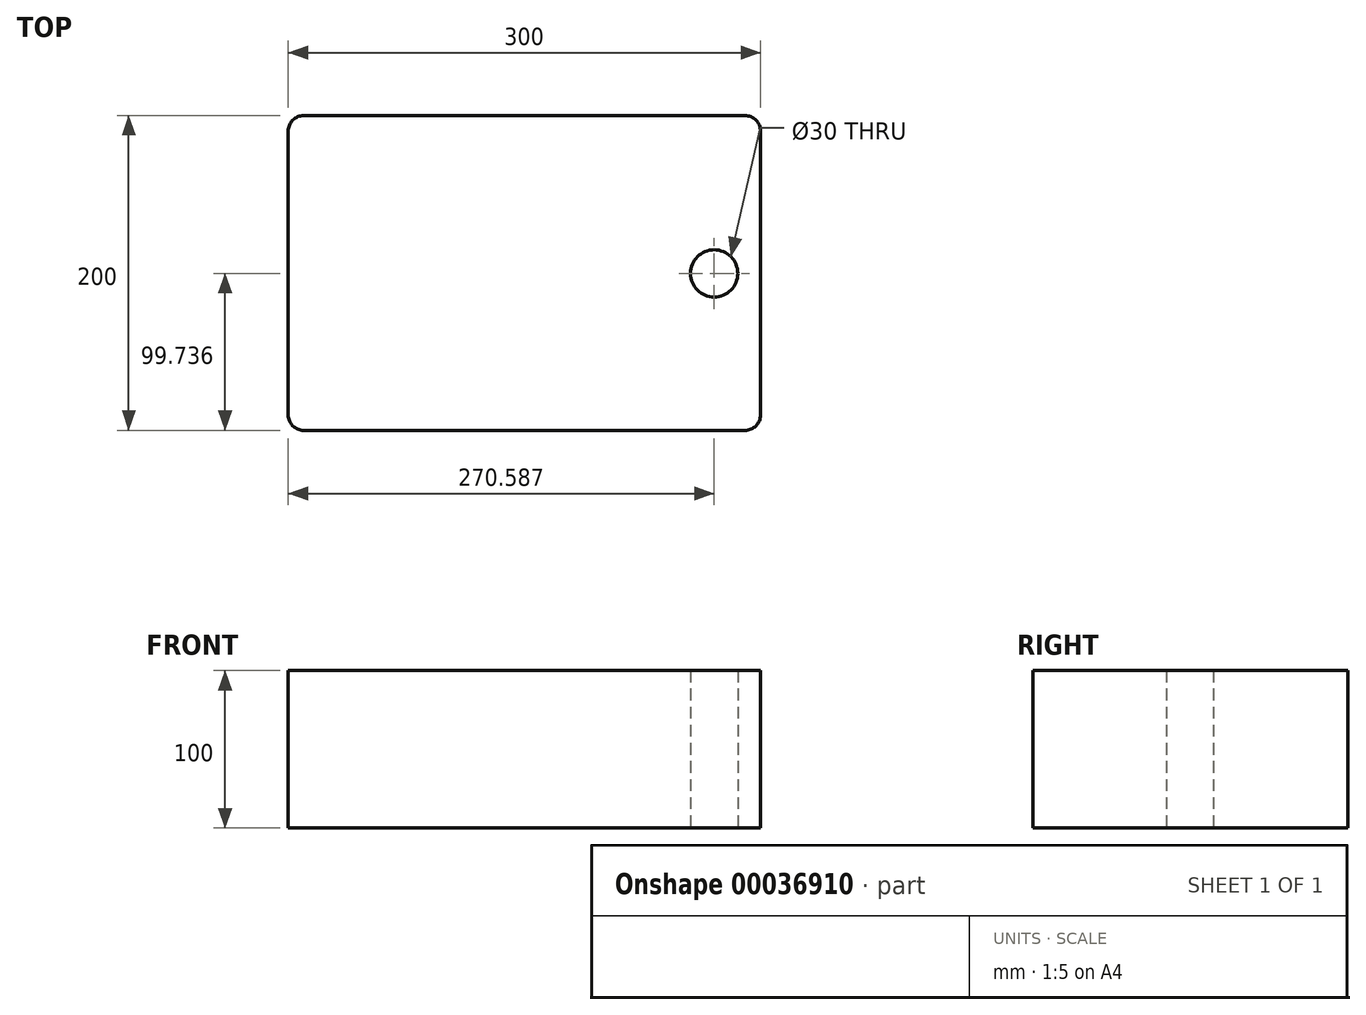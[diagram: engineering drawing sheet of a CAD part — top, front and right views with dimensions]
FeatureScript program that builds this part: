
annotation { "Feature Type Name" : "Feature", "Feature Type Description" : "" }
export const myFeature = defineFeature(function(context is Context, id is Id, definition is map)
    precondition{}
    {
        {
            var Q0;
            Q0=qCreatedBy(makeId("Top.planeOp"),FACE);
            var sketch = newSketch(context, id + "F0", { "sketchPlane" : qUnion([Q0])});
            skLineSegment(sketch, "E0.bottom", {"start": v(-154.92, 124.98) * mm, "end": v(145.08, 124.98) * mm});
            skLineSegment(sketch, "E0.top", {"start": v(-154.92, -75.02) * mm, "end": v(145.08, -75.02) * mm});
            skLineSegment(sketch, "E0.left", {"start": v(-154.92, 124.98) * mm, "end": v(-154.92, -75.02) * mm});
            skLineSegment(sketch, "E0.right", {"start": v(145.08, 124.98) * mm, "end": v(145.08, -75.02) * mm});
            skCircle(sketch, "E1", {"center": v(115.67, 24.72) * mm, "radius": 15 * mm});
            skSolve(sketch);
        }
        {
            var Q0;
            Q0=makeQuery(id+"F0.imprint","IMPRINT",FACE,{"disambiguationData":[TD([[makeQuery(id+"F0.imprint","IMPRINT",EDGE,{"derivedFrom":sQuery(id+"F0.wireOp",EDGE,"E0.bottom")}),-1.0]])]});
            extrude(context, id + "F1", {"entities" : qUnion([Q0]), "depth" : 100 * mm});
        }
        {
            var Q0;
            Q0=makeQuery(id+"F1.opExtrude","SWEPT_EDGE",EDGE,{"disambiguationData":[OSD([sQuery(id+"F0.wireOp",EDGE,"E0.bottom"),sQuery(id+"F0.wireOp",EDGE,"E0.left")])]});
            var Q1;
            Q1=makeQuery(id+"F1.opExtrude","SWEPT_EDGE",EDGE,{"disambiguationData":[OSD([sQuery(id+"F0.wireOp",EDGE,"E0.top"),sQuery(id+"F0.wireOp",EDGE,"E0.left")])]});
            var Q2;
            Q2=makeQuery(id+"F1.opExtrude","SWEPT_EDGE",EDGE,{"disambiguationData":[OSD([sQuery(id+"F0.wireOp",EDGE,"E0.bottom"),sQuery(id+"F0.wireOp",EDGE,"E0.right")])]});
            var Q3;
            Q3=makeQuery(id+"F1.opExtrude","SWEPT_EDGE",EDGE,{"disambiguationData":[OSD([sQuery(id+"F0.wireOp",EDGE,"E0.top"),sQuery(id+"F0.wireOp",EDGE,"E0.right")])]});
            fillet(context, id + "F2", {"entities" : qUnion([Q0, Q1, Q2, Q3]), "radius" : 10 * mm, "tangentPropagation" : true, "allowEdgeOverflow" : false});
        }
    });
